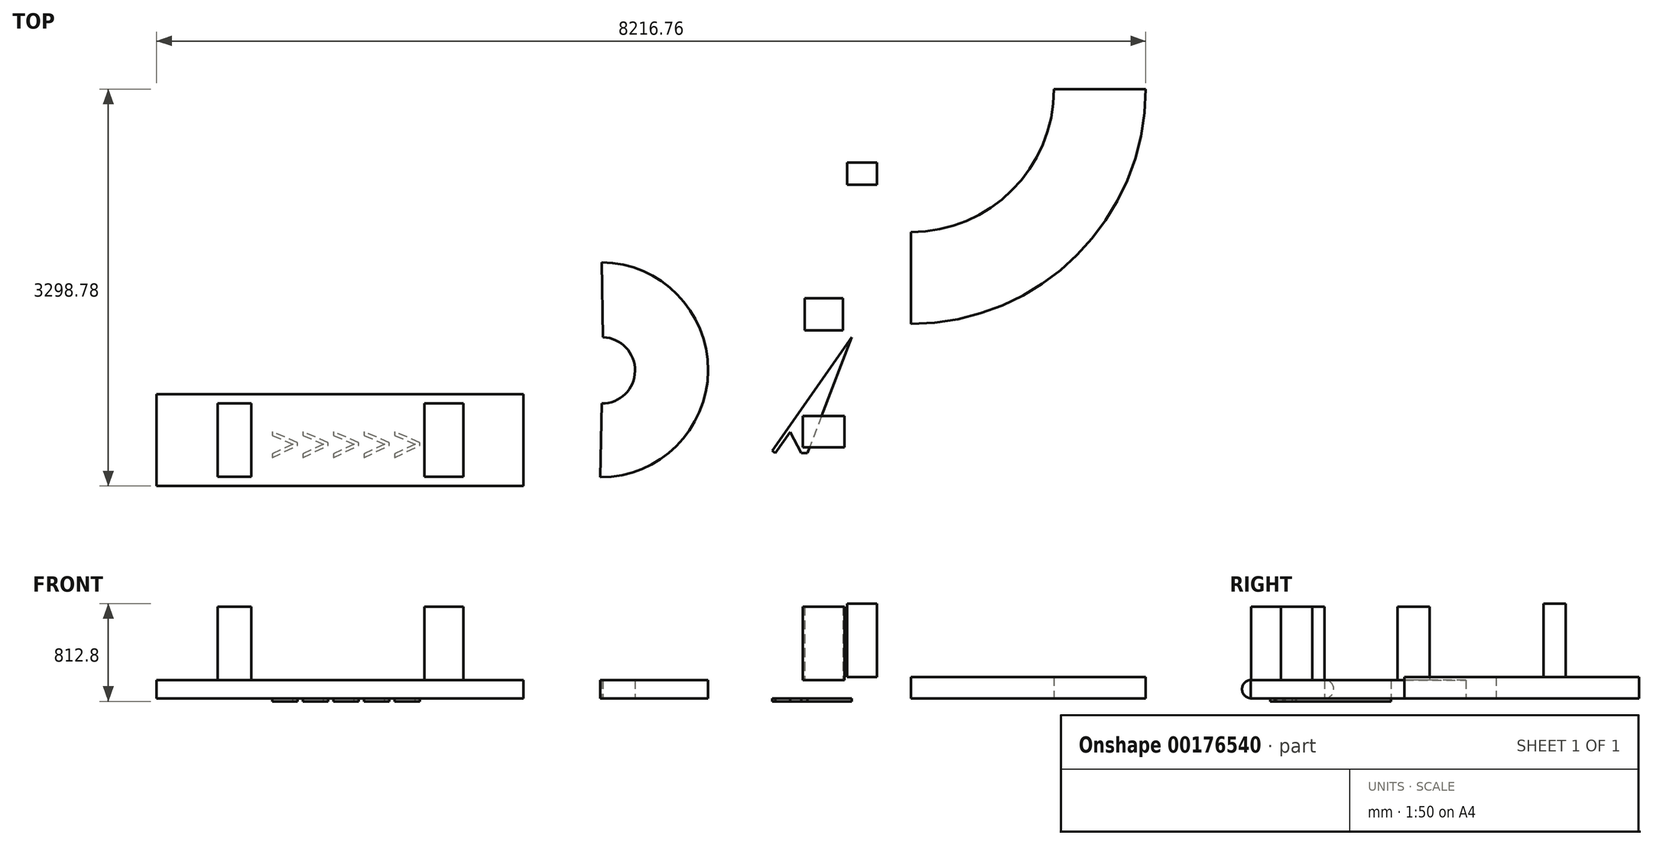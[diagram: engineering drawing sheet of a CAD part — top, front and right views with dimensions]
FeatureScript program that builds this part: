
annotation { "Feature Type Name" : "Feature", "Feature Type Description" : "" }
export const myFeature = defineFeature(function(context is Context, id is Id, definition is map)
    precondition{}
    {
        {
            var Q0;
            Q0=qCreatedBy(makeId("Top.planeOp"),FACE);
            var sketch = newSketch(context, id + "F0", { "sketchPlane" : qUnion([Q0])});
            skLineSegment(sketch, "E0.bottom", {"start": v(-1997.16, 396.69) * mm, "end": v(1050.84, 396.69) * mm});
            skLineSegment(sketch, "E0.top", {"start": v(-1997.16, -365.31) * mm, "end": v(1050.84, -365.31) * mm});
            skLineSegment(sketch, "E0.left", {"start": v(-1997.16, 396.69) * mm, "end": v(-1997.16, -365.31) * mm});
            skLineSegment(sketch, "E0.right", {"start": v(1050.84, 396.69) * mm, "end": v(1050.84, -365.31) * mm});
            skSolve(sketch);
        }
        {
            var Q0;
            Q0=makeQuery(id+"F0.imprint","IMPRINT",FACE,{"disambiguationData":[TD([[makeQuery(id+"F0.imprint","IMPRINT",EDGE,{"derivedFrom":sQuery(id+"F0.wireOp",EDGE,"E0.bottom")}),-1.0]])]});
            extrude(context, id + "F1", {"entities" : qUnion([Q0]), "depth" : 152.4 * mm});
        }
        {
            var Q0;
            Q0=makeQuery(id+"F1.opExtrude","CAP_EDGE",EDGE,{"disambiguationData":[OSD([sQuery(id+"F0.wireOp",EDGE,"E0.top")])],"isStart":true});
            var Q1;
            Q1=makeQuery(id+"F1.opExtrude","CAP_EDGE",EDGE,{"disambiguationData":[OSD([sQuery(id+"F0.wireOp",EDGE,"E0.top")])],"isStart":false});
            var Q2;
            Q2=makeQuery(id+"F1.opExtrude","CAP_EDGE",EDGE,{"disambiguationData":[OSD([sQuery(id+"F0.wireOp",EDGE,"E0.bottom")])],"isStart":true});
            var Q3;
            Q3=makeQuery(id+"F1.opExtrude","CAP_EDGE",EDGE,{"disambiguationData":[OSD([sQuery(id+"F0.wireOp",EDGE,"E0.bottom")])],"isStart":false});
            fillet(context, id + "F2", {"entities" : qUnion([Q0, Q1, Q2, Q3]), "radius" : 76.2 * mm, "tangentPropagation" : true, "allowEdgeOverflow" : false});
        }
        {
            var Q0;
            Q0=makeQuery(id+"F1.opExtrude","CAP_FACE",FACE,{"disambiguationData":[OSD([sQuery(id+"F0.wireOp",EDGE,"E0.bottom"),sQuery(id+"F0.wireOp",EDGE,"E0.top"),sQuery(id+"F0.wireOp",EDGE,"E0.left"),sQuery(id+"F0.wireOp",EDGE,"E0.right")])],"isStart":false});
            var sketch = newSketch(context, id + "F3", { "sketchPlane" : qUnion([Q0])});
            skLineSegment(sketch, "E1.bottom", {"start": v(-1491.47, 320.49) * mm, "end": v(-1211.61, 320.49) * mm});
            skLineSegment(sketch, "E1.top", {"start": v(-1491.47, -289.11) * mm, "end": v(-1211.61, -289.11) * mm});
            skLineSegment(sketch, "E1.left", {"start": v(-1491.47, 320.49) * mm, "end": v(-1491.47, -289.11) * mm});
            skLineSegment(sketch, "E1.right", {"start": v(-1211.61, 320.49) * mm, "end": v(-1211.61, -289.11) * mm});
            skLineSegment(sketch, "E2.bottom", {"start": v(229.12, 320.49) * mm, "end": v(552.03, 320.49) * mm});
            skLineSegment(sketch, "E2.top", {"start": v(229.12, -289.11) * mm, "end": v(552.03, -289.11) * mm});
            skLineSegment(sketch, "E2.left", {"start": v(229.12, 320.49) * mm, "end": v(229.12, -289.11) * mm});
            skLineSegment(sketch, "E2.right", {"start": v(552.03, 320.49) * mm, "end": v(552.03, -289.11) * mm});
            skSolve(sketch);
        }
        {
            var Q0;
            Q0=makeQuery(id+"F3.imprint","IMPRINT",FACE,{"disambiguationData":[TD([[makeQuery(id+"F3.imprint","IMPRINT",EDGE,{"derivedFrom":sQuery(id+"F3.wireOp",EDGE,"E1.bottom")}),1.0]])]});
            var Q1;
            Q1=makeQuery(id+"F3.imprint","IMPRINT",FACE,{"disambiguationData":[TD([[makeQuery(id+"F3.imprint","IMPRINT",EDGE,{"derivedFrom":sQuery(id+"F3.wireOp",EDGE,"E2.bottom")}),1.0]])]});
            extrude(context, id + "F4", {"entities" : qUnion([Q0, Q1]), "operationType" : NewBodyOperationType.ADD, "depth" : 609.6 * mm});
        }
        {
            var Q0;
            Q0=makeQuery(id+"F1.opExtrude","CAP_FACE",FACE,{"disambiguationData":[OSD([sQuery(id+"F0.wireOp",EDGE,"E0.bottom"),sQuery(id+"F0.wireOp",EDGE,"E0.top"),sQuery(id+"F0.wireOp",EDGE,"E0.left"),sQuery(id+"F0.wireOp",EDGE,"E0.right")])],"isStart":true});
            var sketch = newSketch(context, id + "F5", { "sketchPlane" : qUnion([Q0])});
            skText(sketch, "E3", { "text": ">>>>>", "fontName": "OpenSans-Regular.ttf"});
            const initialGuessF5  = {"E3": [-1.05818, -0.13922, 1, 0, 0.31985]};
            skSetInitialGuess(sketch, initialGuessF5);
            skSolve(sketch);
        }
        {
            var Q0;
            Q0 = qSketchRegion(id + "F5", true);
            extrude(context, id + "F6", {"entities" : qUnion([Q0]), "operationType" : NewBodyOperationType.ADD, "depth" : 25.4 * mm});
        }
        {
            var Q0;
            Q0=makeQuery(id+"F1.opExtrude","CAP_FACE",FACE,{"disambiguationData":[OSD([sQuery(id+"F0.wireOp",EDGE,"E0.bottom"),sQuery(id+"F0.wireOp",EDGE,"E0.top"),sQuery(id+"F0.wireOp",EDGE,"E0.left"),sQuery(id+"F0.wireOp",EDGE,"E0.right")])],"isStart":true});
            var sketch = newSketch(context, id + "F7", { "sketchPlane" : qUnion([Q0])});
            skLineSegment(sketch, "E4", {"start": v(1050.84, 289.11) * mm, "end": v(1688.45, 291.42) * mm});
            skArc(sketch, "E5", {"start": v(1688.45, 291.42) * mm, "mid": v(2584.1, -595.1) * mm, "end": v(1700.3, -1493.44) * mm});
            skLineSegment(sketch, "E6", {"start": v(1050.84, -320.49) * mm, "end": v(1701.6, -320.49) * mm});
            skArc(sketch, "E7", {"start": v(1701.6, -320.49) * mm, "mid": v(1976.98, -590.87) * mm, "end": v(1711.67, -871.16) * mm});
            skLineSegment(sketch, "E8", {"start": v(1711.67, -871.16) * mm, "end": v(1700.3, -1493.44) * mm});
            skLineSegment(sketch, "E9", {"start": v(1688.45, 291.42) * mm, "end": v(1701.6, -320.49) * mm});
            skSolve(sketch);
        }
        {
            var Q0;
            Q0 = qSketchRegion(id + "F7", true);
            extrude(context, id + "F8", {"entities" : qUnion([Q0]), "oppositeDirection" : true, "depth" : 152.4 * mm});
        }
        {
            var Q0;
            Q0=makeQuery(id+"F8.opExtrude","CAP_FACE",FACE,{"disambiguationData":[OSD([sQuery(id+"F7.wireOp",EDGE,"E5"),sQuery(id+"F7.wireOp",EDGE,"E7"),sQuery(id+"F7.wireOp",EDGE,"E8"),sQuery(id+"F7.wireOp",EDGE,"E9")])],"isStart":false});
            var sketch = newSketch(context, id + "F9", { "sketchPlane" : qUnion([Q0])});
            skLineSegment(sketch, "E10.bottom", {"start": v(3705.67, 1193.74) * mm, "end": v(3385.8, 1193.74) * mm});
            skLineSegment(sketch, "E10.top", {"start": v(3705.67, 927.98) * mm, "end": v(3385.8, 927.98) * mm});
            skLineSegment(sketch, "E10.left", {"start": v(3705.67, 1193.74) * mm, "end": v(3705.67, 927.98) * mm});
            skLineSegment(sketch, "E10.right", {"start": v(3385.8, 1193.74) * mm, "end": v(3385.8, 927.98) * mm});
            skLineSegment(sketch, "E11.bottom", {"start": v(3716.97, 217.28) * mm, "end": v(3369.74, 217.28) * mm});
            skLineSegment(sketch, "E11.top", {"start": v(3716.97, -42.14) * mm, "end": v(3369.74, -42.14) * mm});
            skLineSegment(sketch, "E11.left", {"start": v(3716.97, 217.28) * mm, "end": v(3716.97, -42.14) * mm});
            skLineSegment(sketch, "E11.right", {"start": v(3369.74, 217.28) * mm, "end": v(3369.74, -42.14) * mm});
            skSolve(sketch);
        }
        {
            var Q0;
            Q0=makeQuery(id+"F9.imprint","IMPRINT",FACE,{"disambiguationData":[TD([[makeQuery(id+"F9.imprint","IMPRINT",EDGE,{"derivedFrom":sQuery(id+"F9.wireOp",EDGE,"E10.bottom")}),1.0]])]});
            var Q1;
            Q1=makeQuery(id+"F9.imprint","IMPRINT",FACE,{"disambiguationData":[TD([[makeQuery(id+"F9.imprint","IMPRINT",EDGE,{"derivedFrom":sQuery(id+"F9.wireOp",EDGE,"E11.bottom")}),1.0]])]});
            var Q2;
            Q2=sQuery(id+"F9.wireOp",EDGE,"E11.top");
            extrude(context, id + "F10", {"entities" : qUnion([Q0, Q1]), "operationType" : NewBodyOperationType.ADD, "surfaceEntities" : qUnion([Q2]), "depth" : 609.6 * mm});
        }
        {
            var Q0;
            Q0=makeQuery(id+"F8.opExtrude","CAP_FACE",FACE,{"disambiguationData":[OSD([sQuery(id+"F7.wireOp",EDGE,"E5"),sQuery(id+"F7.wireOp",EDGE,"E7"),sQuery(id+"F7.wireOp",EDGE,"E8"),sQuery(id+"F7.wireOp",EDGE,"E9")])],"isStart":true});
            var sketch = newSketch(context, id + "F11", { "sketchPlane" : qUnion([Q0])});
            skLineSegment(sketch, "E12", {"start": v(3116.15, 72.45) * mm, "end": v(3777.79, -871.16) * mm});
            skLineSegment(sketch, "E13", {"start": v(3777.79, -871.16) * mm, "end": v(3409.9, 90.6) * mm});
            skLineSegment(sketch, "E14", {"start": v(3116.15, 72.45) * mm, "end": v(3141.67, 90.6) * mm});
            skLineSegment(sketch, "E15", {"start": v(3141.67, 90.6) * mm, "end": v(3265.01, -82.77) * mm});
            skLineSegment(sketch, "E16", {"start": v(3265.01, -82.77) * mm, "end": v(3358.52, 90.6) * mm});
            skLineSegment(sketch, "E17", {"start": v(3358.52, 90.6) * mm, "end": v(3409.9, 90.6) * mm});
            skLineSegment(sketch, "E18", {"start": v(3522.33, -299.68) * mm, "end": v(3713.4, -458.25) * mm});
            skLineSegment(sketch, "E19", {"start": v(3554.86, -263.07) * mm, "end": v(3694.5, -378.96) * mm});
            skPoint(sketch, "E19.endSnap0", {"position": v(3617.86, -378.96) * mm});
            skLineSegment(sketch, "E20", {"start": v(3694.5, -378.96) * mm, "end": v(3750.02, -214.24) * mm});
            skLineSegment(sketch, "E21", {"start": v(3713.4, -458.25) * mm, "end": v(3786.61, -214.23) * mm});
            skLineSegment(sketch, "E22", {"start": v(3750.02, -214.24) * mm, "end": v(3786.61, -214.23) * mm});
            skLineSegment(sketch, "E23", {"start": v(3554.86, -263.07) * mm, "end": v(3522.33, -299.68) * mm});
            skSolve(sketch);
        }
        {
            var Q0;
            Q0=makeQuery(id+"F11.imprint","IMPRINT",FACE,{"disambiguationData":[TD([[makeQuery(id+"F11.imprint","IMPRINT",EDGE,{"derivedFrom":sQuery(id+"F11.wireOp",EDGE,"E18")}),1.0]])]});
            var Q1;
            Q1=makeQuery(id+"F11.imprint","IMPRINT",FACE,{"disambiguationData":[TD([[makeQuery(id+"F11.imprint","IMPRINT",EDGE,{"derivedFrom":sQuery(id+"F11.wireOp",EDGE,"E12")}),1.0]])]});
            extrude(context, id + "F12", {"entities" : qUnion([Q0, Q1]), "operationType" : NewBodyOperationType.ADD, "depth" : 25.4 * mm});
        }
        {
            var Q0;
            Q0=makeQuery(id+"F8.opExtrude","SWEPT_BODY",BODY,{"disambiguationData":[OSD([sQuery(id+"F7.wireOp",EDGE,"E5"),sQuery(id+"F7.wireOp",EDGE,"E7"),sQuery(id+"F7.wireOp",EDGE,"E8"),sQuery(id+"F7.wireOp",EDGE,"E9")])]});
            var Q1;
            Q1=makeQuery(id+"F10.opExtrude","SWEPT_FACE",FACE,{"disambiguationData":[OSD([sQuery(id+"F9.wireOp",EDGE,"E10.bottom")])]});
            transform(context, id + "F13", {"entities" : qUnion([Q0]), "transformType" : TransformType.TRANSLATION_DISTANCE, "transformDirection" : qUnion([Q1]), "distance" : 2133.6 * mm, "makeCopy" : true});
        }
        {
            var Q0;
            Q0=makeQuery(id+"F13.opPattern","COPY",BODY,{"derivedFrom":makeQuery(id+"F8.opExtrude","SWEPT_BODY",BODY,{"disambiguationData":[OSD([sQuery(id+"F7.wireOp",EDGE,"E5"),sQuery(id+"F7.wireOp",EDGE,"E7"),sQuery(id+"F7.wireOp",EDGE,"E8"),sQuery(id+"F7.wireOp",EDGE,"E9")])]}),"instanceName":"1"});
            deleteBodies(context, id + "F14", {"entities" : qUnion([Q0])});
        }
        {
            var Q0;
            Q0=makeQuery(id+"F8.opExtrude","CAP_FACE",FACE,{"disambiguationData":[OSD([sQuery(id+"F7.wireOp",EDGE,"E5"),sQuery(id+"F7.wireOp",EDGE,"E7"),sQuery(id+"F7.wireOp",EDGE,"E8"),sQuery(id+"F7.wireOp",EDGE,"E9")])],"isStart":true});
            var sketch = newSketch(context, id + "F15", { "sketchPlane" : qUnion([Q0])});
            skCircle(sketch, "E24", {"center": v(4268.3, -2933.47) * mm, "radius": 1951.3 * mm});
            skCircle(sketch, "E25", {"center": v(4268.3, -2933.47) * mm, "radius": 1189.3 * mm});
            skLineSegment(sketch, "E26", {"start": v(4268.3, -982.17) * mm, "end": v(4268.3, -1744.17) * mm});
            skLineSegment(sketch, "E27", {"start": v(5457.6, -2933.47) * mm, "end": v(6219.6, -2933.47) * mm});
            skSolve(sketch);
        }
        {
            var Q0;
            {var subQ0=sQuery(id+"F15.wireOp",EDGE,"E26");Q0=makeQuery(id+"F15.imprint","IMPRINT",FACE,{"disambiguationData":[TD([[makeQuery(id+"F15.imprint","IMPRINT",EDGE,{"derivedFrom":subQ0}),1.0]])]});}
            extrude(context, id + "F16", {"entities" : qUnion([Q0]), "oppositeDirection" : true, "depth" : 177.8 * mm});
        }
        {
            var Q0;
            Q0=makeQuery(id+"F16.opExtrude","CAP_FACE",FACE,{"disambiguationData":[OSD([sQuery(id+"F15.wireOp",EDGE,"E24"),sQuery(id+"F15.wireOp",EDGE,"E25"),sQuery(id+"F15.wireOp",EDGE,"E26"),sQuery(id+"F15.wireOp",EDGE,"E27")])],"isStart":false});
            var sketch = newSketch(context, id + "F17", { "sketchPlane" : qUnion([Q0])});
            skLineSegment(sketch, "E28.bottom", {"start": v(3738.73, 2139.46) * mm, "end": v(3987.94, 2139.46) * mm});
            skLineSegment(sketch, "E28.top", {"start": v(3738.73, 2322.7) * mm, "end": v(3987.94, 2322.7) * mm});
            skLineSegment(sketch, "E28.left", {"start": v(3738.73, 2139.46) * mm, "end": v(3738.73, 2322.7) * mm});
            skLineSegment(sketch, "E28.right", {"start": v(3987.94, 2139.46) * mm, "end": v(3987.94, 2322.7) * mm});
            skSolve(sketch);
        }
        {
            var Q0;
            Q0=makeQuery(id+"F17.imprint","IMPRINT",FACE,{"disambiguationData":[TD([[makeQuery(id+"F17.imprint","IMPRINT",EDGE,{"derivedFrom":sQuery(id+"F17.wireOp",EDGE,"E28.bottom")}),1.0]])]});
            extrude(context, id + "F18", {"entities" : qUnion([Q0]), "operationType" : NewBodyOperationType.ADD, "depth" : 609.6 * mm});
        }
    });
